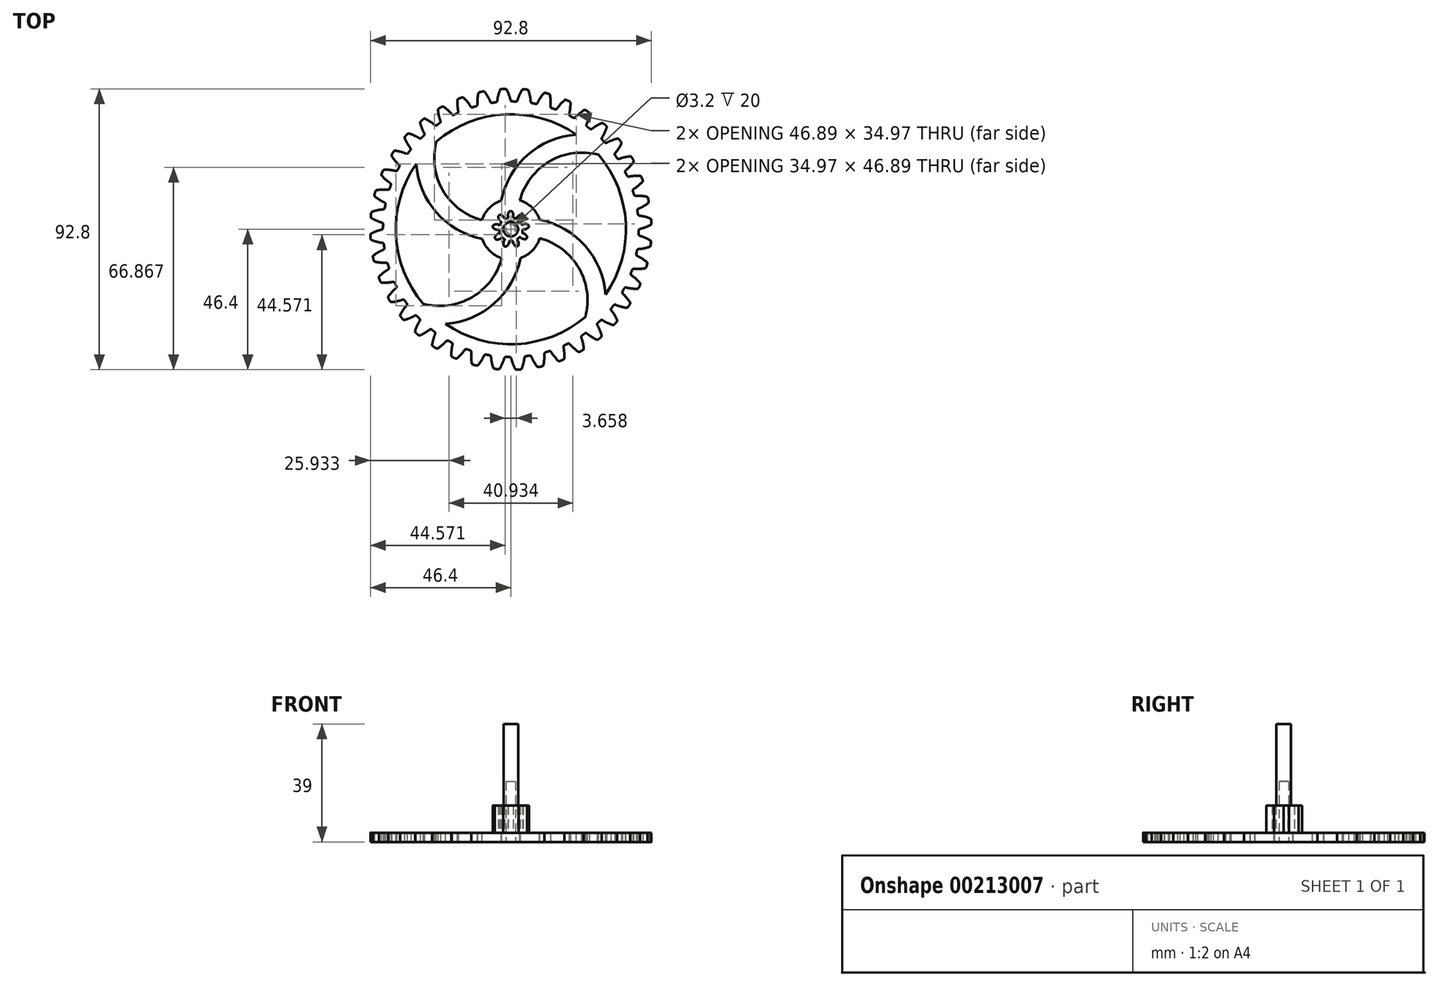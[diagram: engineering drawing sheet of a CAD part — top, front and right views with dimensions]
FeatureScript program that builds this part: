
annotation { "Feature Type Name" : "Feature", "Feature Type Description" : "" }
export const myFeature = defineFeature(function(context is Context, id is Id, definition is map)
    precondition{}
    {
        {
            var Q0;
            Q0=qCreatedBy(makeId("Top.planeOp"),FACE);
            var sketch = newSketch(context, id + "F0", { "sketchPlane" : qUnion([Q0])});
            skCircle(sketch, "E0", {"center": v(0, 0) * mm, "radius": 20.88 * mm, "construction": true});
            skLineSegment(sketch, "E1", {"start": v(0, 0) * mm, "end": v(20.88, 0) * mm, "construction": true});
            skLineSegment(sketch, "E2", {"start": v(20.88, 0) * mm, "end": v(20.88, 0) * mm});
            skLineSegment(sketch, "E3", {"start": v(0, 0) * mm, "end": v(20.86, 1.06) * mm, "construction": true});
            skLineSegment(sketch, "E4", {"start": v(20.86, 1.06) * mm, "end": v(20.9, 0) * mm, "construction": true});
            skLineSegment(sketch, "E5", {"start": v(0, 0) * mm, "end": v(20.78, 2.11) * mm, "construction": true});
            skLineSegment(sketch, "E6", {"start": v(20.78, 2.11) * mm, "end": v(20.99, 0) * mm, "construction": true});
            skLineSegment(sketch, "E7", {"start": v(0, 0) * mm, "end": v(20.64, 3.16) * mm, "construction": true});
            skLineSegment(sketch, "E8", {"start": v(20.64, 3.16) * mm, "end": v(21.12, 0.02) * mm, "construction": true});
            skLineSegment(sketch, "E9", {"start": v(0, 0) * mm, "end": v(20.46, 4.2) * mm, "construction": true});
            skLineSegment(sketch, "E10", {"start": v(20.46, 4.2) * mm, "end": v(21.3, 0.06) * mm, "construction": true});
            skLineSegment(sketch, "E11", {"start": v(0, 0) * mm, "end": v(20.22, 5.23) * mm, "construction": true});
            skLineSegment(sketch, "E12", {"start": v(20.22, 5.23) * mm, "end": v(21.54, 0.11) * mm, "construction": true});
            skLineSegment(sketch, "E13", {"start": v(0, 0) * mm, "end": v(19.93, 6.24) * mm, "construction": true});
            skLineSegment(sketch, "E14", {"start": v(19.93, 6.24) * mm, "end": v(21.82, 0.2) * mm, "construction": true});
            skLineSegment(sketch, "E15", {"start": v(0, 0) * mm, "end": v(19.59, 7.24) * mm, "construction": true});
            skLineSegment(sketch, "E16", {"start": v(19.59, 7.24) * mm, "end": v(22.15, 0.3) * mm, "construction": true});
            skLineSegment(sketch, "E17", {"start": v(0, 0) * mm, "end": v(19.2, 8.23) * mm, "construction": true});
            skLineSegment(sketch, "E18", {"start": v(19.2, 8.23) * mm, "end": v(22.52, 0.45) * mm, "construction": true});
            skLineSegment(sketch, "E19", {"start": v(0, 0) * mm, "end": v(18.75, 9.19) * mm, "construction": true});
            skLineSegment(sketch, "E20", {"start": v(18.75, 9.19) * mm, "end": v(22.94, 0.64) * mm, "construction": true});
            skLineSegment(sketch, "E21", {"start": v(0, 0) * mm, "end": v(18.26, 10.12) * mm, "construction": true});
            skLineSegment(sketch, "E22", {"start": v(18.26, 10.12) * mm, "end": v(23.39, 0.88) * mm, "construction": true});
            skPoint(sketch, "E23", {"position": v(20.88, 0) * mm});
            skCircle(sketch, "E24", {"center": v(0, 0) * mm, "radius": 21.11 * mm});
            skLineSegment(sketch, "E25", {"start": v(0, 0) * mm, "end": v(32.51, 1.76) * mm, "construction": true});
            skFitSpline(sketch, "E26", {"points": [v(20.88, 0) * mm, v(20.9, 0) * mm, v(20.99, 0) * mm, v(21.12, 0.02) * mm, v(21.3, 0.06) * mm, v(21.54, 0.11) * mm, v(21.82, 0.2) * mm, v(22.15, 0.3) * mm, v(22.52, 0.45) * mm, v(22.94, 0.64) * mm, v(23.39, 0.88) * mm], "startDerivative": vector(0.7, 0.02) * mm, "endDerivative": vector(3.1, 1.66) * mm, "construction": true});
            skFitSpline(sketch, "E27", {"points": [v(20.88, 0) * mm, v(20.9, 0) * mm, v(20.99, 0) * mm, v(21.12, 0.02) * mm, v(21.3, 0.06) * mm, v(21.54, 0.11) * mm, v(21.82, 0.2) * mm, v(22.15, 0.3) * mm, v(22.52, 0.45) * mm, v(22.94, 0.64) * mm, v(23.39, 0.88) * mm], "startDerivative": vector(0.7, 0.02) * mm, "endDerivative": vector(3.1, 1.66) * mm});
            skFitSpline(sketch, "E28", {"points": [v(20.88, 0) * mm, v(20.9, 0) * mm, v(20.99, 0) * mm, v(21.12, 0.02) * mm, v(21.3, 0.06) * mm, v(21.54, 0.11) * mm, v(21.82, 0.2) * mm, v(22.15, 0.3) * mm, v(22.52, 0.45) * mm, v(22.94, 0.64) * mm, v(23.39, 0.88) * mm], "startDerivative": vector(0.7, 0.02) * mm, "endDerivative": vector(3.1, 1.66) * mm, "construction": true});
            skFitSpline(sketch, "E29.MirrorCS", {"points": [v(20.76, 2.26) * mm, v(20.79, 2.26) * mm, v(20.87, 2.26) * mm, v(21, 2.26) * mm, v(21.19, 2.25) * mm, v(21.43, 2.22) * mm, v(21.72, 2.17) * mm, v(22.06, 2.1) * mm, v(22.44, 1.98) * mm, v(22.87, 1.84) * mm, v(23.35, 1.65) * mm], "startDerivative": vector(0.7, 0.06) * mm, "endDerivative": vector(3.27, -1.32) * mm, "construction": true});
            skFitSpline(sketch, "E30.MirrorCS", {"points": [v(20.76, 2.26) * mm, v(20.79, 2.26) * mm, v(20.87, 2.26) * mm, v(21, 2.26) * mm, v(21.19, 2.25) * mm, v(21.43, 2.22) * mm, v(21.72, 2.17) * mm, v(22.06, 2.1) * mm, v(22.44, 1.98) * mm, v(22.87, 1.84) * mm, v(23.35, 1.65) * mm], "startDerivative": vector(0.7, 0.06) * mm, "endDerivative": vector(3.27, -1.32) * mm});
            skArc(sketch, "E31", {"start": v(23.16, 1.73) * mm, "mid": v(-23.19, -1.26) * mm, "end": v(23.2, 0.78) * mm, "construction": true});
            skArc(sketch, "E32", {"start": v(23.2, 0.78) * mm, "mid": v(23.19, 1.26) * mm, "end": v(23.16, 1.73) * mm});
            skSolve(sketch);
        }
        {
            var Q0;
            Q0=qCreatedBy(makeId("Front.planeOp"),FACE);
            var sketch = newSketch(context, id + "F1", { "sketchPlane" : qUnion([Q0])});
            skLineSegment(sketch, "E33", {"start": v(0, 0) * mm, "end": v(0, 19.36) * mm});
            skSolve(sketch);
        }
        {
            var Q0;
            {var subQ0=sQuery(id+"F0.wireOp",EDGE,"E24");var subQ1=makeQuery(id+"F0.imprint","INTERSECT",VERTEX,{"derivedFrom":[subQ0,sQuery(id+"F0.wireOp",EDGE,"E27")]});Q0=makeQuery(id+"F0.imprint","IMPRINT",FACE,{"disambiguationData":[TD([[makeQuery(id+"F0.imprint","IMPRINT",EDGE,{"disambiguationData":[TD([[subQ1,-1.0]])],"derivedFrom":subQ0}),1.0]])]});}
            var Q1;
            {var subQ0=sQuery(id+"F0.wireOp",EDGE,"E27");Q1=makeQuery(id+"F0.imprint","IMPRINT",FACE,{"disambiguationData":[TD([[makeQuery(id+"F0.imprint","IMPRINT",EDGE,{"derivedFrom":subQ0}),1.0]])]});}
            extrude(context, id + "F2", {"entities" : qUnion([Q0, Q1]), "depth" : 1.5 * mm});
        }
        {
            var Q0;
            Q0=makeQuery(id+"F2.opExtrude","SWEPT_EDGE",EDGE,{"disambiguationData":[OSD([sQuery(id+"F0.wireOp",EDGE,"E24"),sQuery(id+"F0.wireOp",EDGE,"E27")])]});
            var Q1;
            Q1=makeQuery(id+"F2.opExtrude","SWEPT_EDGE",EDGE,{"disambiguationData":[OSD([sQuery(id+"F0.wireOp",EDGE,"E27"),sQuery(id+"F0.wireOp",EDGE,"E32")])]});
            var Q2;
            Q2=makeQuery(id+"F2.opExtrude","SWEPT_EDGE",EDGE,{"disambiguationData":[OSD([sQuery(id+"F0.wireOp",EDGE,"E30.MirrorCS"),sQuery(id+"F0.wireOp",EDGE,"E32")])]});
            var Q3;
            Q3=makeQuery(id+"F2.opExtrude","SWEPT_EDGE",EDGE,{"disambiguationData":[OSD([sQuery(id+"F0.wireOp",EDGE,"E24"),sQuery(id+"F0.wireOp",EDGE,"E30.MirrorCS")])]});
            fillet(context, id + "F3", {"entities" : qUnion([Q0, Q1, Q2, Q3]), "radius" : 0.3 * mm, "tangentPropagation" : true, "allowEdgeOverflow" : false});
        }
        {
            var Q0;
            Q0=makeQuery(id+"F2.opExtrude","SWEPT_BODY",BODY,{"disambiguationData":[OSD([sQuery(id+"F0.wireOp",EDGE,"E24"),sQuery(id+"F0.wireOp",EDGE,"E27"),sQuery(id+"F0.wireOp",EDGE,"E30.MirrorCS"),sQuery(id+"F0.wireOp",EDGE,"E32")])]});
            var Q1;
            Q1=sQuery(id+"F1.wireOp",EDGE,"E33");
            circularPattern(context, id + "F4", {"operationType" : NewBodyOperationType.ADD, "entities" : qUnion([Q0]), "axis" : qUnion([Q1]), "angle" : 360 * degree, "instanceCount" : 40, "equalSpace" : true, "fullFeaturePattern" : false});
        }
        {
            var Q0;
            Q0=makeQuery(id+"F2.opExtrude","SWEPT_BODY",BODY,{"disambiguationData":[OSD([sQuery(id+"F0.wireOp",EDGE,"E24"),sQuery(id+"F0.wireOp",EDGE,"E27"),sQuery(id+"F0.wireOp",EDGE,"E30.MirrorCS"),sQuery(id+"F0.wireOp",EDGE,"E32")])]});
            var Q1;
            Q1=sQuery(id+"F1.wireOp",VERTEX,"E33.start");
            transform(context, id + "F5", {"entities" : qUnion([Q0]), "transformType" : TransformType.SCALE_UNIFORMLY, "scale" : 2, "scalePoint" : qUnion([Q1]), "makeCopy" : false});
        }
        {
            var Q0;
            {var subQ0=makeQuery(id+"F2.opExtrude","CAP_FACE",FACE,{"disambiguationData":[OSD([sQuery(id+"F0.wireOp",EDGE,"E24"),sQuery(id+"F0.wireOp",EDGE,"E27"),sQuery(id+"F0.wireOp",EDGE,"E30.MirrorCS"),sQuery(id+"F0.wireOp",EDGE,"E32")])],"isStart":false});Q0=makeQuery(id+"F4.boolean.opBoolean","MERGE",FACE,{"derivedFrom":[subQ0,makeQuery(id+"F4.opPattern","COPY",FACE,{"derivedFrom":subQ0,"instanceName":"1"}),makeQuery(id+"F4.opPattern","COPY",FACE,{"derivedFrom":subQ0,"instanceName":"2"}),makeQuery(id+"F4.opPattern","COPY",FACE,{"derivedFrom":subQ0,"instanceName":"3"}),makeQuery(id+"F4.opPattern","COPY",FACE,{"derivedFrom":subQ0,"instanceName":"4"}),makeQuery(id+"F4.opPattern","COPY",FACE,{"derivedFrom":subQ0,"instanceName":"5"}),makeQuery(id+"F4.opPattern","COPY",FACE,{"derivedFrom":subQ0,"instanceName":"6"}),makeQuery(id+"F4.opPattern","COPY",FACE,{"derivedFrom":subQ0,"instanceName":"7"}),makeQuery(id+"F4.opPattern","COPY",FACE,{"derivedFrom":subQ0,"instanceName":"8"}),makeQuery(id+"F4.opPattern","COPY",FACE,{"derivedFrom":subQ0,"instanceName":"9"}),makeQuery(id+"F4.opPattern","COPY",FACE,{"derivedFrom":subQ0,"instanceName":"10"}),makeQuery(id+"F4.opPattern","COPY",FACE,{"derivedFrom":subQ0,"instanceName":"11"}),makeQuery(id+"F4.opPattern","COPY",FACE,{"derivedFrom":subQ0,"instanceName":"12"}),makeQuery(id+"F4.opPattern","COPY",FACE,{"derivedFrom":subQ0,"instanceName":"13"}),makeQuery(id+"F4.opPattern","COPY",FACE,{"derivedFrom":subQ0,"instanceName":"14"}),makeQuery(id+"F4.opPattern","COPY",FACE,{"derivedFrom":subQ0,"instanceName":"15"}),makeQuery(id+"F4.opPattern","COPY",FACE,{"derivedFrom":subQ0,"instanceName":"16"}),makeQuery(id+"F4.opPattern","COPY",FACE,{"derivedFrom":subQ0,"instanceName":"17"}),makeQuery(id+"F4.opPattern","COPY",FACE,{"derivedFrom":subQ0,"instanceName":"18"}),makeQuery(id+"F4.opPattern","COPY",FACE,{"derivedFrom":subQ0,"instanceName":"19"}),makeQuery(id+"F4.opPattern","COPY",FACE,{"derivedFrom":subQ0,"instanceName":"20"}),makeQuery(id+"F4.opPattern","COPY",FACE,{"derivedFrom":subQ0,"instanceName":"21"}),makeQuery(id+"F4.opPattern","COPY",FACE,{"derivedFrom":subQ0,"instanceName":"22"}),makeQuery(id+"F4.opPattern","COPY",FACE,{"derivedFrom":subQ0,"instanceName":"23"}),makeQuery(id+"F4.opPattern","COPY",FACE,{"derivedFrom":subQ0,"instanceName":"24"}),makeQuery(id+"F4.opPattern","COPY",FACE,{"derivedFrom":subQ0,"instanceName":"25"}),makeQuery(id+"F4.opPattern","COPY",FACE,{"derivedFrom":subQ0,"instanceName":"26"}),makeQuery(id+"F4.opPattern","COPY",FACE,{"derivedFrom":subQ0,"instanceName":"27"}),makeQuery(id+"F4.opPattern","COPY",FACE,{"derivedFrom":subQ0,"instanceName":"28"}),makeQuery(id+"F4.opPattern","COPY",FACE,{"derivedFrom":subQ0,"instanceName":"29"}),makeQuery(id+"F4.opPattern","COPY",FACE,{"derivedFrom":subQ0,"instanceName":"30"}),makeQuery(id+"F4.opPattern","COPY",FACE,{"derivedFrom":subQ0,"instanceName":"31"}),makeQuery(id+"F4.opPattern","COPY",FACE,{"derivedFrom":subQ0,"instanceName":"32"}),makeQuery(id+"F4.opPattern","COPY",FACE,{"derivedFrom":subQ0,"instanceName":"33"}),makeQuery(id+"F4.opPattern","COPY",FACE,{"derivedFrom":subQ0,"instanceName":"34"}),makeQuery(id+"F4.opPattern","COPY",FACE,{"derivedFrom":subQ0,"instanceName":"35"}),makeQuery(id+"F4.opPattern","COPY",FACE,{"derivedFrom":subQ0,"instanceName":"36"}),makeQuery(id+"F4.opPattern","COPY",FACE,{"derivedFrom":subQ0,"instanceName":"37"}),makeQuery(id+"F4.opPattern","COPY",FACE,{"derivedFrom":subQ0,"instanceName":"38"}),makeQuery(id+"F4.opPattern","COPY",FACE,{"derivedFrom":subQ0,"instanceName":"39"})]});}
            var sketch = newSketch(context, id + "F6", { "sketchPlane" : qUnion([Q0])});
            skCircle(sketch, "E34", {"center": v(0, 0) * mm, "radius": 4.7 * mm, "construction": true});
            skLineSegment(sketch, "E35", {"start": v(0, 0) * mm, "end": v(4.68, 0.38) * mm, "construction": true});
            skLineSegment(sketch, "E36", {"start": v(4.68, 0.38) * mm, "end": v(4.71, 0) * mm, "construction": true});
            skLineSegment(sketch, "E37", {"start": v(0, 0) * mm, "end": v(4.64, 0.75) * mm, "construction": true});
            skLineSegment(sketch, "E38", {"start": v(4.64, 0.75) * mm, "end": v(4.76, 0) * mm, "construction": true});
            skLineSegment(sketch, "E39", {"start": v(0, 0) * mm, "end": v(4.56, 1.12) * mm, "construction": true});
            skLineSegment(sketch, "E40", {"start": v(4.56, 1.12) * mm, "end": v(4.83, 0.02) * mm, "construction": true});
            skLineSegment(sketch, "E41", {"start": v(0, 0) * mm, "end": v(4.46, 1.48) * mm, "construction": true});
            skLineSegment(sketch, "E42", {"start": v(4.46, 1.48) * mm, "end": v(4.93, 0.05) * mm, "construction": true});
            skLineSegment(sketch, "E43", {"start": v(0, 0) * mm, "end": v(4.32, 1.84) * mm, "construction": true});
            skLineSegment(sketch, "E44", {"start": v(4.32, 1.84) * mm, "end": v(5.06, 0.1) * mm, "construction": true});
            skLineSegment(sketch, "E45", {"start": v(0, 0) * mm, "end": v(4.16, 2.18) * mm, "construction": true});
            skLineSegment(sketch, "E46", {"start": v(4.16, 2.18) * mm, "end": v(5.21, 0.17) * mm, "construction": true});
            skLineSegment(sketch, "E47", {"start": v(0, 0) * mm, "end": v(3.98, 2.5) * mm, "construction": true});
            skLineSegment(sketch, "E48", {"start": v(3.98, 2.5) * mm, "end": v(5.38, 0.27) * mm, "construction": true});
            skLineSegment(sketch, "E49", {"start": v(0, 0) * mm, "end": v(3.76, 2.81) * mm, "construction": true});
            skLineSegment(sketch, "E50", {"start": v(3.76, 2.81) * mm, "end": v(5.57, 0.4) * mm, "construction": true});
            skLineSegment(sketch, "E51", {"start": v(0, 0) * mm, "end": v(3.52, 3.1) * mm, "construction": true});
            skLineSegment(sketch, "E52", {"start": v(3.52, 3.1) * mm, "end": v(5.77, 0.56) * mm, "construction": true});
            skLineSegment(sketch, "E53", {"start": v(0, 0) * mm, "end": v(3.26, 3.38) * mm, "construction": true});
            skLineSegment(sketch, "E54", {"start": v(3.26, 3.38) * mm, "end": v(5.98, 0.76) * mm, "construction": true});
            skPoint(sketch, "E55", {"position": v(4.7, 0) * mm});
            skCircle(sketch, "E56", {"center": v(0, 0) * mm, "radius": 3.89 * mm});
            skLineSegment(sketch, "E57", {"start": v(3.89, 0) * mm, "end": v(4.7, 0) * mm});
            skFitSpline(sketch, "E58", {"points": [v(4.7, 0) * mm, v(4.71, 0) * mm, v(4.76, 0) * mm, v(4.83, 0.02) * mm, v(4.93, 0.05) * mm, v(5.06, 0.1) * mm, v(5.21, 0.17) * mm, v(5.38, 0.27) * mm, v(5.57, 0.4) * mm, v(5.77, 0.56) * mm, v(5.98, 0.76) * mm], "startDerivative": vector(0.58, 0) * mm, "endDerivative": vector(1.32, 1.28) * mm});
            skPoint(sketch, "E59", {"position": v(5.95, 0.74) * mm});
            skFitSpline(sketch, "E60", {"points": [v(4.7, 0) * mm, v(4.71, 0) * mm, v(4.76, 0) * mm, v(4.83, 0.02) * mm, v(4.93, 0.05) * mm, v(5.06, 0.1) * mm, v(5.21, 0.17) * mm, v(5.38, 0.27) * mm, v(5.57, 0.4) * mm, v(5.77, 0.56) * mm, v(5.98, 0.76) * mm], "startDerivative": vector(0.58, 0) * mm, "endDerivative": vector(1.32, 1.28) * mm, "construction": true});
            skLineSegment(sketch, "E61", {"start": v(0, 0) * mm, "end": v(7.88, 1.51) * mm, "construction": true});
            skLineSegment(sketch, "E62.MirrorCS", {"start": v(3.61, 1.44) * mm, "end": v(4.37, 1.74) * mm});
            skFitSpline(sketch, "E63.MirrorCS", {"points": [v(4.37, 1.74) * mm, v(4.38, 1.74) * mm, v(4.42, 1.75) * mm, v(4.5, 1.77) * mm, v(4.6, 1.78) * mm, v(4.74, 1.78) * mm, v(4.9, 1.77) * mm, v(5.1, 1.74) * mm, v(5.32, 1.7) * mm, v(5.57, 1.61) * mm, v(5.83, 1.5) * mm], "startDerivative": vector(0.54, 0.22) * mm, "endDerivative": vector(1.7, -0.7) * mm});
            skArc(sketch, "E64", {"start": v(5.8, 1.52) * mm, "mid": v(-5.9, -1.13) * mm, "end": v(5.95, 0.74) * mm, "construction": true});
            skArc(sketch, "E65", {"start": v(5.95, 0.74) * mm, "mid": v(5.9, 1.13) * mm, "end": v(5.8, 1.52) * mm});
            skSolve(sketch);
        }
        {
            var Q0;
            {var subQ1=sQuery(id+"F6.wireOp",EDGE,"E57");Q0=makeQuery(id+"F6.imprint","IMPRINT",FACE,{"disambiguationData":[TD([[makeQuery(id+"F6.imprint","IMPRINT",EDGE,{"derivedFrom":subQ1}),1.0]])]});}
            var Q1;
            {var subQ0=sQuery(id+"F6.wireOp",EDGE,"E56");var subQ1=makeQuery(id+"F6.imprint","INTERSECT",VERTEX,{"derivedFrom":[subQ0,sQuery(id+"F6.wireOp",EDGE,"E57")]});Q1=makeQuery(id+"F6.imprint","IMPRINT",FACE,{"disambiguationData":[TD([[makeQuery(id+"F6.imprint","IMPRINT",EDGE,{"disambiguationData":[TD([[subQ1,-1.0]])],"derivedFrom":subQ0}),1.0]])]});}
            extrude(context, id + "F7", {"entities" : qUnion([Q0, Q1]), "depth" : 9 * mm});
        }
        {
            var Q0;
            Q0=makeQuery(id+"F7.opExtrude","SWEPT_EDGE",EDGE,{"disambiguationData":[OSD([sQuery(id+"F6.wireOp",EDGE,"E56"),sQuery(id+"F6.wireOp",EDGE,"E57")])]});
            var Q1;
            Q1=makeQuery(id+"F7.opExtrude","SWEPT_EDGE",EDGE,{"disambiguationData":[OSD([sQuery(id+"F6.wireOp",EDGE,"E58"),sQuery(id+"F6.wireOp",EDGE,"E65")])]});
            var Q2;
            Q2=makeQuery(id+"F7.opExtrude","SWEPT_EDGE",EDGE,{"disambiguationData":[OSD([sQuery(id+"F6.wireOp",EDGE,"E63.MirrorCS"),sQuery(id+"F6.wireOp",EDGE,"E65")])]});
            var Q3;
            Q3=makeQuery(id+"F7.opExtrude","SWEPT_EDGE",EDGE,{"disambiguationData":[OSD([sQuery(id+"F6.wireOp",EDGE,"E56"),sQuery(id+"F6.wireOp",EDGE,"E62.MirrorCS")])]});
            fillet(context, id + "F8", {"entities" : qUnion([Q0, Q1, Q2, Q3]), "radius" : 0.3 * mm, "tangentPropagation" : true, "allowEdgeOverflow" : false});
        }
        {
            var Q0;
            Q0=makeQuery(id+"F7.opExtrude","SWEPT_BODY",BODY,{"disambiguationData":[OSD([sQuery(id+"F6.wireOp",EDGE,"E56"),sQuery(id+"F6.wireOp",EDGE,"E57"),sQuery(id+"F6.wireOp",EDGE,"E58"),sQuery(id+"F6.wireOp",EDGE,"E62.MirrorCS"),sQuery(id+"F6.wireOp",EDGE,"E63.MirrorCS"),sQuery(id+"F6.wireOp",EDGE,"E65")])]});
            var Q1;
            Q1=sQuery(id+"F1.wireOp",EDGE,"E33");
            circularPattern(context, id + "F9", {"operationType" : NewBodyOperationType.ADD, "entities" : qUnion([Q0]), "axis" : qUnion([Q1]), "angle" : 360 * degree, "instanceCount" : 9, "equalSpace" : true});
        }
        {
            var Q0;
            {var subQ0=makeQuery(id+"F7.opExtrude","CAP_FACE",FACE,{"disambiguationData":[OSD([sQuery(id+"F6.wireOp",EDGE,"E56"),sQuery(id+"F6.wireOp",EDGE,"E57"),sQuery(id+"F6.wireOp",EDGE,"E58"),sQuery(id+"F6.wireOp",EDGE,"E62.MirrorCS"),sQuery(id+"F6.wireOp",EDGE,"E63.MirrorCS"),sQuery(id+"F6.wireOp",EDGE,"E65")])],"isStart":false});Q0=makeQuery(id+"F9.boolean.opBoolean","MERGE",FACE,{"derivedFrom":[subQ0,makeQuery(id+"F9.opPattern","COPY",FACE,{"derivedFrom":subQ0,"instanceName":"1"}),makeQuery(id+"F9.opPattern","COPY",FACE,{"derivedFrom":subQ0,"instanceName":"2"}),makeQuery(id+"F9.opPattern","COPY",FACE,{"derivedFrom":subQ0,"instanceName":"3"}),makeQuery(id+"F9.opPattern","COPY",FACE,{"derivedFrom":subQ0,"instanceName":"4"}),makeQuery(id+"F9.opPattern","COPY",FACE,{"derivedFrom":subQ0,"instanceName":"5"}),makeQuery(id+"F9.opPattern","COPY",FACE,{"derivedFrom":subQ0,"instanceName":"6"}),makeQuery(id+"F9.opPattern","COPY",FACE,{"derivedFrom":subQ0,"instanceName":"7"}),makeQuery(id+"F9.opPattern","COPY",FACE,{"derivedFrom":subQ0,"instanceName":"8"})]});}
            var sketch = newSketch(context, id + "F10", { "sketchPlane" : qUnion([Q0])});
            skCircle(sketch, "E66", {"center": v(0, 0) * mm, "radius": 2.4 * mm});
            skSolve(sketch);
        }
        {
            var Q0;
            Q0=makeQuery(id+"F10.imprint","IMPRINT",FACE,{"disambiguationData":[TD([[makeQuery(id+"F10.imprint","IMPRINT",EDGE,{"derivedFrom":sQuery(id+"F10.wireOp",EDGE,"E66")}),1.0]])]});
            extrude(context, id + "F11", {"entities" : qUnion([Q0]), "operationType" : NewBodyOperationType.ADD, "depth" : 27 * mm});
        }
        {
            var Q0;
            {var subQ0=makeQuery(id+"F2.opExtrude","CAP_FACE",FACE,{"disambiguationData":[OSD([sQuery(id+"F0.wireOp",EDGE,"E24"),sQuery(id+"F0.wireOp",EDGE,"E27"),sQuery(id+"F0.wireOp",EDGE,"E30.MirrorCS"),sQuery(id+"F0.wireOp",EDGE,"E32")])],"isStart":false});Q0=makeQuery(id+"F4.boolean.opBoolean","MERGE",FACE,{"derivedFrom":[subQ0,makeQuery(id+"F4.opPattern","COPY",FACE,{"derivedFrom":subQ0,"instanceName":"1"}),makeQuery(id+"F4.opPattern","COPY",FACE,{"derivedFrom":subQ0,"instanceName":"2"}),makeQuery(id+"F4.opPattern","COPY",FACE,{"derivedFrom":subQ0,"instanceName":"3"}),makeQuery(id+"F4.opPattern","COPY",FACE,{"derivedFrom":subQ0,"instanceName":"4"}),makeQuery(id+"F4.opPattern","COPY",FACE,{"derivedFrom":subQ0,"instanceName":"5"}),makeQuery(id+"F4.opPattern","COPY",FACE,{"derivedFrom":subQ0,"instanceName":"6"}),makeQuery(id+"F4.opPattern","COPY",FACE,{"derivedFrom":subQ0,"instanceName":"7"}),makeQuery(id+"F4.opPattern","COPY",FACE,{"derivedFrom":subQ0,"instanceName":"8"}),makeQuery(id+"F4.opPattern","COPY",FACE,{"derivedFrom":subQ0,"instanceName":"9"}),makeQuery(id+"F4.opPattern","COPY",FACE,{"derivedFrom":subQ0,"instanceName":"10"}),makeQuery(id+"F4.opPattern","COPY",FACE,{"derivedFrom":subQ0,"instanceName":"11"}),makeQuery(id+"F4.opPattern","COPY",FACE,{"derivedFrom":subQ0,"instanceName":"12"}),makeQuery(id+"F4.opPattern","COPY",FACE,{"derivedFrom":subQ0,"instanceName":"13"}),makeQuery(id+"F4.opPattern","COPY",FACE,{"derivedFrom":subQ0,"instanceName":"14"}),makeQuery(id+"F4.opPattern","COPY",FACE,{"derivedFrom":subQ0,"instanceName":"15"}),makeQuery(id+"F4.opPattern","COPY",FACE,{"derivedFrom":subQ0,"instanceName":"16"}),makeQuery(id+"F4.opPattern","COPY",FACE,{"derivedFrom":subQ0,"instanceName":"17"}),makeQuery(id+"F4.opPattern","COPY",FACE,{"derivedFrom":subQ0,"instanceName":"18"}),makeQuery(id+"F4.opPattern","COPY",FACE,{"derivedFrom":subQ0,"instanceName":"19"}),makeQuery(id+"F4.opPattern","COPY",FACE,{"derivedFrom":subQ0,"instanceName":"20"}),makeQuery(id+"F4.opPattern","COPY",FACE,{"derivedFrom":subQ0,"instanceName":"21"}),makeQuery(id+"F4.opPattern","COPY",FACE,{"derivedFrom":subQ0,"instanceName":"22"}),makeQuery(id+"F4.opPattern","COPY",FACE,{"derivedFrom":subQ0,"instanceName":"23"}),makeQuery(id+"F4.opPattern","COPY",FACE,{"derivedFrom":subQ0,"instanceName":"24"}),makeQuery(id+"F4.opPattern","COPY",FACE,{"derivedFrom":subQ0,"instanceName":"25"}),makeQuery(id+"F4.opPattern","COPY",FACE,{"derivedFrom":subQ0,"instanceName":"26"}),makeQuery(id+"F4.opPattern","COPY",FACE,{"derivedFrom":subQ0,"instanceName":"27"}),makeQuery(id+"F4.opPattern","COPY",FACE,{"derivedFrom":subQ0,"instanceName":"28"}),makeQuery(id+"F4.opPattern","COPY",FACE,{"derivedFrom":subQ0,"instanceName":"29"}),makeQuery(id+"F4.opPattern","COPY",FACE,{"derivedFrom":subQ0,"instanceName":"30"}),makeQuery(id+"F4.opPattern","COPY",FACE,{"derivedFrom":subQ0,"instanceName":"31"}),makeQuery(id+"F4.opPattern","COPY",FACE,{"derivedFrom":subQ0,"instanceName":"32"}),makeQuery(id+"F4.opPattern","COPY",FACE,{"derivedFrom":subQ0,"instanceName":"33"}),makeQuery(id+"F4.opPattern","COPY",FACE,{"derivedFrom":subQ0,"instanceName":"34"}),makeQuery(id+"F4.opPattern","COPY",FACE,{"derivedFrom":subQ0,"instanceName":"35"}),makeQuery(id+"F4.opPattern","COPY",FACE,{"derivedFrom":subQ0,"instanceName":"36"}),makeQuery(id+"F4.opPattern","COPY",FACE,{"derivedFrom":subQ0,"instanceName":"37"}),makeQuery(id+"F4.opPattern","COPY",FACE,{"derivedFrom":subQ0,"instanceName":"38"}),makeQuery(id+"F4.opPattern","COPY",FACE,{"derivedFrom":subQ0,"instanceName":"39"})]});}
            var sketch = newSketch(context, id + "F12", { "sketchPlane" : qUnion([Q0])});
            skCircle(sketch, "E67", {"center": v(0, 0) * mm, "radius": 10 * mm});
            skCircle(sketch, "E68", {"center": v(0, 0) * mm, "radius": 38 * mm});
            skLineSegment(sketch, "E69", {"start": v(0, 0) * mm, "end": v(25.43, 28.24) * mm, "construction": true});
            skCircle(sketch, "E70", {"center": v(23.48, 4.1) * mm, "radius": 24.2 * mm, "construction": true});
            skPoint(sketch, "E70.first.point", {"position": v(0, 10) * mm});
            skPoint(sketch, "E70.third.point", {"position": v(14.17, 26.46) * mm});
            skArc(sketch, "E71", {"start": v(21.62, 31.25) * mm, "mid": v(5.53, 24.56) * mm, "end": v(-3.2, 9.48) * mm});
            skArc(sketch, "E72", {"start": v(28.97, 24.6) * mm, "mid": v(12.85, 22.46) * mm, "end": v(2.98, 9.55) * mm});
            skArc(sketch, "E73.1.0", {"start": v(-31.25, 21.62) * mm, "mid": v(-24.56, 5.53) * mm, "end": v(-9.48, -3.2) * mm});
            skArc(sketch, "E73.1.1", {"start": v(-24.6, 28.97) * mm, "mid": v(-22.46, 12.85) * mm, "end": v(-9.55, 2.98) * mm});
            skArc(sketch, "E73.2.0", {"start": v(-21.62, -31.25) * mm, "mid": v(-5.53, -24.56) * mm, "end": v(3.2, -9.48) * mm});
            skArc(sketch, "E73.2.1", {"start": v(-28.97, -24.6) * mm, "mid": v(-12.85, -22.46) * mm, "end": v(-2.98, -9.55) * mm});
            skArc(sketch, "E73.3.0", {"start": v(31.25, -21.62) * mm, "mid": v(24.56, -5.53) * mm, "end": v(9.48, 3.2) * mm});
            skArc(sketch, "E73.3.1", {"start": v(24.6, -28.97) * mm, "mid": v(22.46, -12.85) * mm, "end": v(9.55, -2.98) * mm});
            skSolve(sketch);
        }
        {
            var Q0;
            {var subQ0=sQuery(id+"F12.wireOp",EDGE,"E71");Q0=makeQuery(id+"F12.imprint","IMPRINT",FACE,{"disambiguationData":[TD([[makeQuery(id+"F12.imprint","IMPRINT",EDGE,{"derivedFrom":subQ0}),-1.0]])]});}
            var Q1;
            {var subQ0=sQuery(id+"F12.wireOp",EDGE,"E73.1.0");Q1=makeQuery(id+"F12.imprint","IMPRINT",FACE,{"disambiguationData":[TD([[makeQuery(id+"F12.imprint","IMPRINT",EDGE,{"derivedFrom":subQ0}),-1.0]])]});}
            var Q2;
            {var subQ0=sQuery(id+"F12.wireOp",EDGE,"E73.2.0");Q2=makeQuery(id+"F12.imprint","IMPRINT",FACE,{"disambiguationData":[TD([[makeQuery(id+"F12.imprint","IMPRINT",EDGE,{"derivedFrom":subQ0}),-1.0]])]});}
            var Q3;
            {var subQ0=sQuery(id+"F12.wireOp",EDGE,"E72");Q3=makeQuery(id+"F12.imprint","IMPRINT",FACE,{"disambiguationData":[TD([[makeQuery(id+"F12.imprint","IMPRINT",EDGE,{"derivedFrom":subQ0}),1.0]])]});}
            extrude(context, id + "F13", {"entities" : qUnion([Q0, Q1, Q2, Q3]), "operationType" : NewBodyOperationType.REMOVE, "endBound" : BoundingType.UP_TO_NEXT, "oppositeDirection" : true, "depth" : 25 * mm});
        }
        {
            var Q0;
            {var subQ0=makeQuery(id+"F2.opExtrude","CAP_FACE",FACE,{"disambiguationData":[OSD([sQuery(id+"F0.wireOp",EDGE,"E24"),sQuery(id+"F0.wireOp",EDGE,"E27"),sQuery(id+"F0.wireOp",EDGE,"E30.MirrorCS"),sQuery(id+"F0.wireOp",EDGE,"E32")])],"isStart":true});Q0=makeQuery(id+"F4.boolean.opBoolean","MERGE",FACE,{"derivedFrom":[subQ0,makeQuery(id+"F4.opPattern","COPY",FACE,{"derivedFrom":subQ0,"instanceName":"1"}),makeQuery(id+"F4.opPattern","COPY",FACE,{"derivedFrom":subQ0,"instanceName":"2"}),makeQuery(id+"F4.opPattern","COPY",FACE,{"derivedFrom":subQ0,"instanceName":"3"}),makeQuery(id+"F4.opPattern","COPY",FACE,{"derivedFrom":subQ0,"instanceName":"4"}),makeQuery(id+"F4.opPattern","COPY",FACE,{"derivedFrom":subQ0,"instanceName":"5"}),makeQuery(id+"F4.opPattern","COPY",FACE,{"derivedFrom":subQ0,"instanceName":"6"}),makeQuery(id+"F4.opPattern","COPY",FACE,{"derivedFrom":subQ0,"instanceName":"7"}),makeQuery(id+"F4.opPattern","COPY",FACE,{"derivedFrom":subQ0,"instanceName":"8"}),makeQuery(id+"F4.opPattern","COPY",FACE,{"derivedFrom":subQ0,"instanceName":"9"}),makeQuery(id+"F4.opPattern","COPY",FACE,{"derivedFrom":subQ0,"instanceName":"10"}),makeQuery(id+"F4.opPattern","COPY",FACE,{"derivedFrom":subQ0,"instanceName":"11"}),makeQuery(id+"F4.opPattern","COPY",FACE,{"derivedFrom":subQ0,"instanceName":"12"}),makeQuery(id+"F4.opPattern","COPY",FACE,{"derivedFrom":subQ0,"instanceName":"13"}),makeQuery(id+"F4.opPattern","COPY",FACE,{"derivedFrom":subQ0,"instanceName":"14"}),makeQuery(id+"F4.opPattern","COPY",FACE,{"derivedFrom":subQ0,"instanceName":"15"}),makeQuery(id+"F4.opPattern","COPY",FACE,{"derivedFrom":subQ0,"instanceName":"16"}),makeQuery(id+"F4.opPattern","COPY",FACE,{"derivedFrom":subQ0,"instanceName":"17"}),makeQuery(id+"F4.opPattern","COPY",FACE,{"derivedFrom":subQ0,"instanceName":"18"}),makeQuery(id+"F4.opPattern","COPY",FACE,{"derivedFrom":subQ0,"instanceName":"19"}),makeQuery(id+"F4.opPattern","COPY",FACE,{"derivedFrom":subQ0,"instanceName":"20"}),makeQuery(id+"F4.opPattern","COPY",FACE,{"derivedFrom":subQ0,"instanceName":"21"}),makeQuery(id+"F4.opPattern","COPY",FACE,{"derivedFrom":subQ0,"instanceName":"22"}),makeQuery(id+"F4.opPattern","COPY",FACE,{"derivedFrom":subQ0,"instanceName":"23"}),makeQuery(id+"F4.opPattern","COPY",FACE,{"derivedFrom":subQ0,"instanceName":"24"}),makeQuery(id+"F4.opPattern","COPY",FACE,{"derivedFrom":subQ0,"instanceName":"25"}),makeQuery(id+"F4.opPattern","COPY",FACE,{"derivedFrom":subQ0,"instanceName":"26"}),makeQuery(id+"F4.opPattern","COPY",FACE,{"derivedFrom":subQ0,"instanceName":"27"}),makeQuery(id+"F4.opPattern","COPY",FACE,{"derivedFrom":subQ0,"instanceName":"28"}),makeQuery(id+"F4.opPattern","COPY",FACE,{"derivedFrom":subQ0,"instanceName":"29"}),makeQuery(id+"F4.opPattern","COPY",FACE,{"derivedFrom":subQ0,"instanceName":"30"}),makeQuery(id+"F4.opPattern","COPY",FACE,{"derivedFrom":subQ0,"instanceName":"31"}),makeQuery(id+"F4.opPattern","COPY",FACE,{"derivedFrom":subQ0,"instanceName":"32"}),makeQuery(id+"F4.opPattern","COPY",FACE,{"derivedFrom":subQ0,"instanceName":"33"}),makeQuery(id+"F4.opPattern","COPY",FACE,{"derivedFrom":subQ0,"instanceName":"34"}),makeQuery(id+"F4.opPattern","COPY",FACE,{"derivedFrom":subQ0,"instanceName":"35"}),makeQuery(id+"F4.opPattern","COPY",FACE,{"derivedFrom":subQ0,"instanceName":"36"}),makeQuery(id+"F4.opPattern","COPY",FACE,{"derivedFrom":subQ0,"instanceName":"37"}),makeQuery(id+"F4.opPattern","COPY",FACE,{"derivedFrom":subQ0,"instanceName":"38"}),makeQuery(id+"F4.opPattern","COPY",FACE,{"derivedFrom":subQ0,"instanceName":"39"})]});}
            var sketch = newSketch(context, id + "F14", { "sketchPlane" : qUnion([Q0])});
            skCircle(sketch, "E74", {"center": v(0, 0) * mm, "radius": 1.6 * mm});
            skSolve(sketch);
        }
        {
            var Q0;
            Q0 = qSketchRegion(id + "F14", true);
            extrude(context, id + "F15", {"entities" : qUnion([Q0]), "operationType" : NewBodyOperationType.REMOVE, "oppositeDirection" : true, "depth" : 20 * mm});
        }
    });
